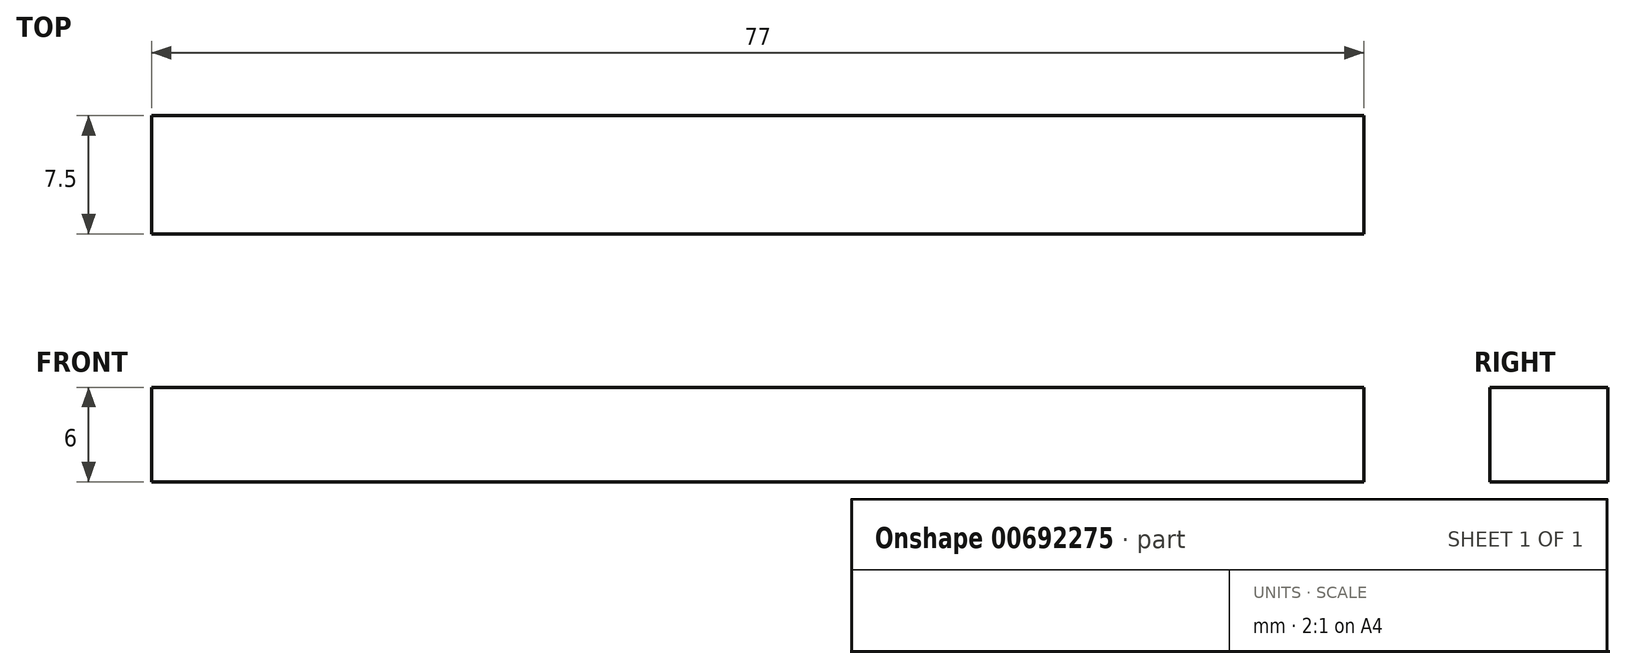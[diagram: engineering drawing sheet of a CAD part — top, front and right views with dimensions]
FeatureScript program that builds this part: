
annotation { "Feature Type Name" : "Feature", "Feature Type Description" : "" }
export const myFeature = defineFeature(function(context is Context, id is Id, definition is map)
    precondition{}
    {
        {
            var Q0;
            Q0=qCreatedBy(makeId("Top.planeOp"),FACE);
            var sketch = newSketch(context, id + "F0", { "sketchPlane" : qUnion([Q0])});
            skLineSegment(sketch, "E0.bottom", {"start": v(0, 0) * mm, "end": v(77, 0) * mm});
            skLineSegment(sketch, "E0.top", {"start": v(0, 7.5) * mm, "end": v(77, 7.5) * mm});
            skLineSegment(sketch, "E0.left", {"start": v(0, 0) * mm, "end": v(0, 7.5) * mm});
            skLineSegment(sketch, "E0.right", {"start": v(77, 0) * mm, "end": v(77, 7.5) * mm});
            skSolve(sketch);
        }
        {
            var Q0;
            Q0 = qSketchRegion(id + "F0", true);
            extrude(context, id + "F1", {"entities" : qUnion([Q0]), "depth" : 6 * mm, "offsetDistance" : 25.4 * mm});
        }
    });
